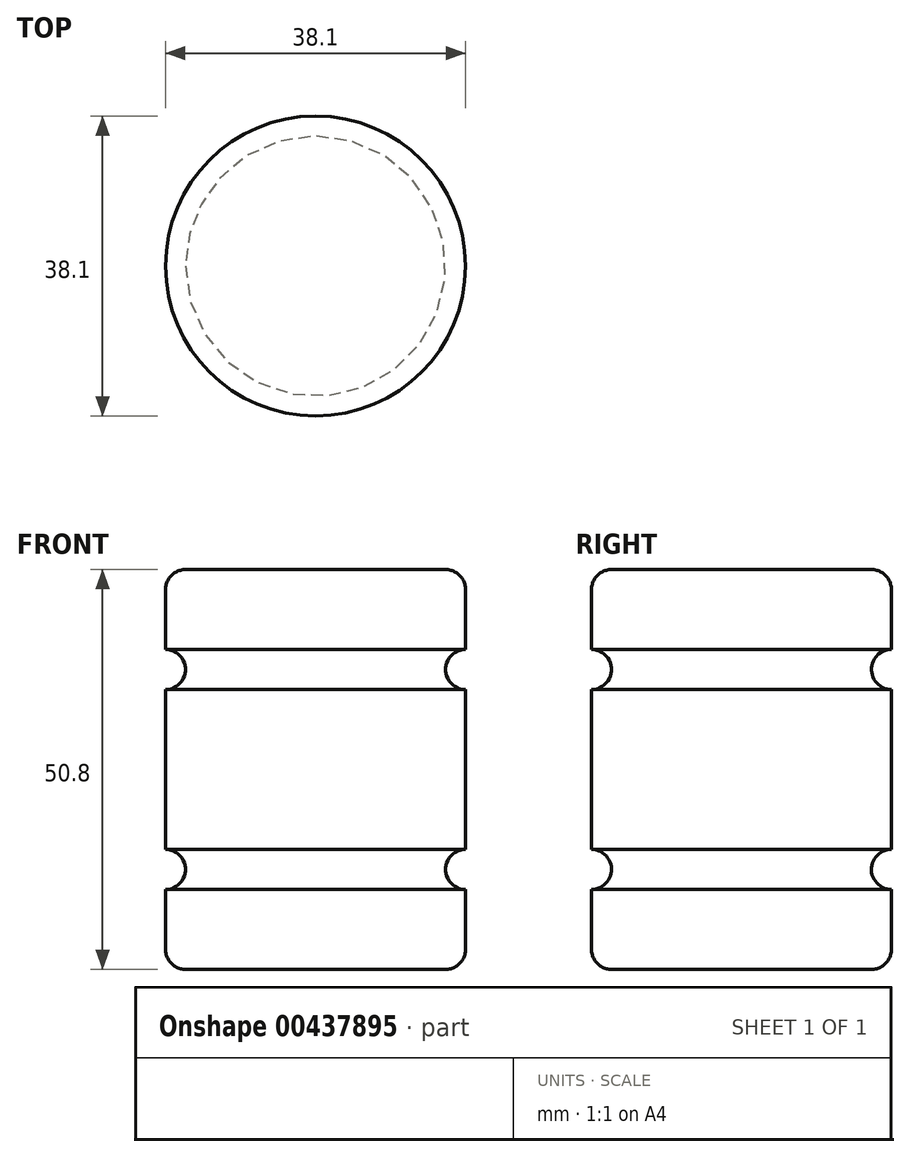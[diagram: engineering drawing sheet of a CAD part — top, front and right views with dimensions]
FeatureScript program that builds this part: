
annotation { "Feature Type Name" : "Feature", "Feature Type Description" : "" }
export const myFeature = defineFeature(function(context is Context, id is Id, definition is map)
    precondition{}
    {
        {
            var Q0;
            Q0=qCreatedBy(makeId("Front.planeOp"),FACE);
            var sketch = newSketch(context, id + "F0", { "sketchPlane" : qUnion([Q0])});
            skLineSegment(sketch, "E0.bottom", {"start": v(0, 0) * mm, "end": v(-19.05, 0) * mm});
            skLineSegment(sketch, "E0.top", {"start": v(0, 50.8) * mm, "end": v(-19.05, 50.8) * mm});
            skLineSegment(sketch, "E0.left", {"start": v(0, 0) * mm, "end": v(0, 10.16) * mm});
            skLineSegment(sketch, "E0.right", {"start": v(-19.05, 0) * mm, "end": v(-19.05, 50.8) * mm});
            skArc(sketch, "E1", {"start": v(0, 40.64) * mm, "mid": v(-2.54, 38.1) * mm, "end": v(0, 35.56) * mm});
            skArc(sketch, "E2", {"start": v(0, 15.24) * mm, "mid": v(-2.54, 12.7) * mm, "end": v(0, 10.16) * mm});
            skLineSegment(sketch, "E3.trimOffspring", {"start": v(0, 40.64) * mm, "end": v(0, 50.8) * mm});
            skLineSegment(sketch, "E4.trimOffspring", {"start": v(0, 15.24) * mm, "end": v(0, 35.56) * mm});
            skSolve(sketch);
        }
        {
            var Q0;
            Q0 = qSketchRegion(id + "F0", true);
            var Q1;
            Q1=sQuery(id+"F0.wireOp",EDGE,"E0.right");
            revolve(context, id + "F1", {"entities" : qUnion([Q0]), "axis" : qUnion([Q1]), "revolveType" : RevolveType.FULL});
        }
        {
            var Q0;
            Q0=makeQuery(id+"F1.opRevolve","SWEPT_FACE",FACE,{"disambiguationData":[OSD([sQuery(id+"F0.wireOp",EDGE,"E0.top")])]});
            var Q1;
            Q1=makeQuery(id+"F1.opRevolve","SWEPT_FACE",FACE,{"disambiguationData":[OSD([sQuery(id+"F0.wireOp",EDGE,"E0.bottom")])]});
            fillet(context, id + "F2", {"entities" : qUnion([Q0, Q1]), "radius" : 2.57 * mm, "tangentPropagation" : true, "allowEdgeOverflow" : false});
        }
    });
